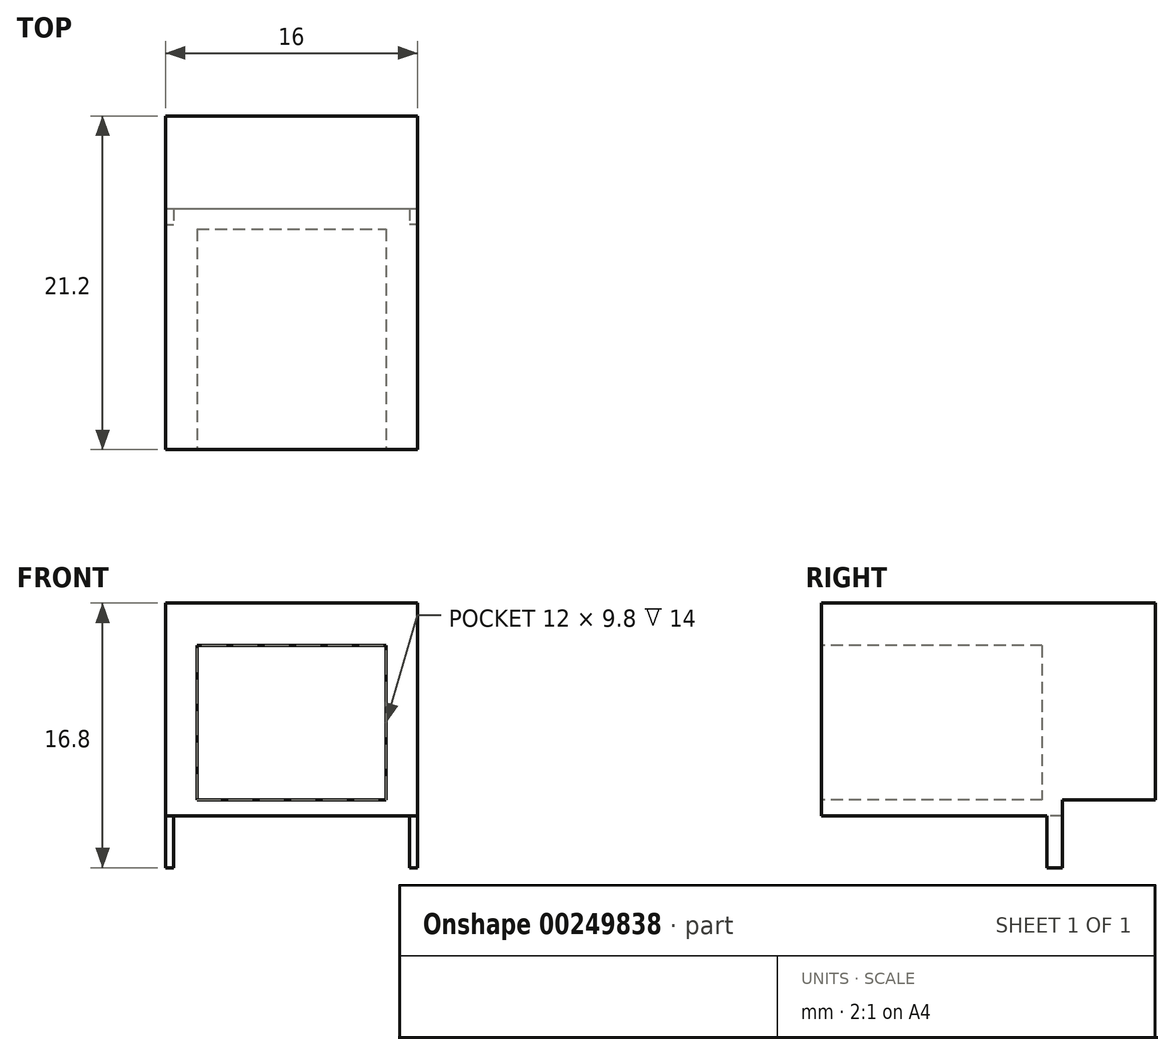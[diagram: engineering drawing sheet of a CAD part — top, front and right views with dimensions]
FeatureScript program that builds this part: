
annotation { "Feature Type Name" : "Feature", "Feature Type Description" : "" }
export const myFeature = defineFeature(function(context is Context, id is Id, definition is map)
    precondition{}
    {
        {
            var Q0;
            Q0=qCreatedBy(makeId("Top.planeOp"),FACE);
            var sketch = newSketch(context, id + "F0", { "sketchPlane" : qUnion([Q0])});
            skLineSegment(sketch, "E0.bottom", {"start": v(0, 0) * mm, "end": v(16, 0) * mm});
            skLineSegment(sketch, "E0.top", {"start": v(0, 21.2) * mm, "end": v(16, 21.2) * mm});
            skLineSegment(sketch, "E0.left", {"start": v(0, 0) * mm, "end": v(0, 21.2) * mm});
            skLineSegment(sketch, "E0.right", {"start": v(16, 0) * mm, "end": v(16, 21.2) * mm});
            skSolve(sketch);
        }
        {
            var Q0;
            Q0 = qSketchRegion(id + "F0", true);
            extrude(context, id + "F1", {"entities" : qUnion([Q0]), "depth" : 13.5 * mm});
        }
        {
            var Q0;
            Q0=makeQuery(id+"F1.opExtrude","SWEPT_FACE",FACE,{"disambiguationData":[OSD([sQuery(id+"F0.wireOp",EDGE,"E0.right")])]});
            var sketch = newSketch(context, id + "F2", { "sketchPlane" : qUnion([Q0])});
            skLineSegment(sketch, "E1.bottom", {"start": v(21.2, 0) * mm, "end": v(15.3, 0) * mm});
            skLineSegment(sketch, "E1.top", {"start": v(21.2, 1) * mm, "end": v(15.3, 1) * mm});
            skLineSegment(sketch, "E1.left", {"start": v(21.2, 0) * mm, "end": v(21.2, 1) * mm});
            skLineSegment(sketch, "E1.right", {"start": v(15.3, 0) * mm, "end": v(15.3, 1) * mm});
            skSolve(sketch);
        }
        {
            var Q0;
            Q0 = qSketchRegion(id + "F2", true);
            extrude(context, id + "F3", {"entities" : qUnion([Q0]), "operationType" : NewBodyOperationType.REMOVE, "endBound" : BoundingType.UP_TO_NEXT, "oppositeDirection" : true, "depth" : 25 * mm});
        }
        {
            var Q0;
            Q0=makeQuery(id+"F1.opExtrude","SWEPT_FACE",FACE,{"disambiguationData":[OSD([sQuery(id+"F0.wireOp",EDGE,"E0.bottom")])]});
            var sketch = newSketch(context, id + "F4", { "sketchPlane" : qUnion([Q0])});
            skLineSegment(sketch, "E2.bottom", {"start": v(2, 10.8) * mm, "end": v(14, 10.8) * mm});
            skLineSegment(sketch, "E2.top", {"start": v(2, 1) * mm, "end": v(14, 1) * mm});
            skLineSegment(sketch, "E2.left", {"start": v(2, 10.8) * mm, "end": v(2, 1) * mm});
            skLineSegment(sketch, "E2.right", {"start": v(14, 10.8) * mm, "end": v(14, 1) * mm});
            skSolve(sketch);
        }
        {
            var Q0;
            Q0 = qSketchRegion(id + "F4", true);
            extrude(context, id + "F5", {"entities" : qUnion([Q0]), "operationType" : NewBodyOperationType.REMOVE, "oppositeDirection" : true, "depth" : 14 * mm});
        }
        {
            var Q0;
            Q0=makeQuery(id+"F1.opExtrude","CAP_FACE",FACE,{"disambiguationData":[OSD([sQuery(id+"F0.wireOp",EDGE,"E0.bottom"),sQuery(id+"F0.wireOp",EDGE,"E0.top"),sQuery(id+"F0.wireOp",EDGE,"E0.left"),sQuery(id+"F0.wireOp",EDGE,"E0.right")])],"isStart":true});
            var sketch = newSketch(context, id + "F6", { "sketchPlane" : qUnion([Q0])});
            skLineSegment(sketch, "E3.bottom", {"start": v(0, -15.3) * mm, "end": v(0.5, -15.3) * mm});
            skLineSegment(sketch, "E3.top", {"start": v(0, -14.3) * mm, "end": v(0.5, -14.3) * mm});
            skLineSegment(sketch, "E3.left", {"start": v(0, -15.3) * mm, "end": v(0, -14.3) * mm});
            skLineSegment(sketch, "E3.right", {"start": v(0.5, -15.3) * mm, "end": v(0.5, -14.3) * mm});
            skLineSegment(sketch, "E4.bottom", {"start": v(16, -15.3) * mm, "end": v(15.5, -15.3) * mm});
            skLineSegment(sketch, "E4.top", {"start": v(16, -14.3) * mm, "end": v(15.5, -14.3) * mm});
            skLineSegment(sketch, "E4.left", {"start": v(16, -15.3) * mm, "end": v(16, -14.3) * mm});
            skLineSegment(sketch, "E4.right", {"start": v(15.5, -15.3) * mm, "end": v(15.5, -14.3) * mm});
            skSolve(sketch);
        }
        {
            var Q0;
            Q0 = qSketchRegion(id + "F6", true);
            extrude(context, id + "F7", {"entities" : qUnion([Q0]), "operationType" : NewBodyOperationType.ADD, "depth" : 3.3 * mm});
        }
    });
